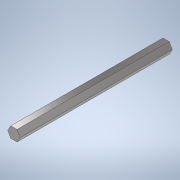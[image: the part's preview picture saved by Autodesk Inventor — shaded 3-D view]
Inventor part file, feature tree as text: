
AUTODESK INVENTOR PART (.ipt)
format: ipt  version: 2020 (Build 240168000, 168)  size: 100,352 bytes
history: native  units: in
note: dims shown in document units (in); Inventor stores cm internally (conversion verified against a paired STEP export)
features: extrude x1, sketch x1
ambient origin geometry x8: Origin, YZ Plane, XZ Plane, XY Plane, X Axis, Y Axis, Z Axis, Center Point
bodies: Solid1 (feature_tree)
feature tree (2):
  extrude  "Extrusion1"  Depth=7.0in TaperAngle=0.0deg
  sketch  "Sketch1"  dims[d0=0.5in d1=7.0in d2=0.0in]
